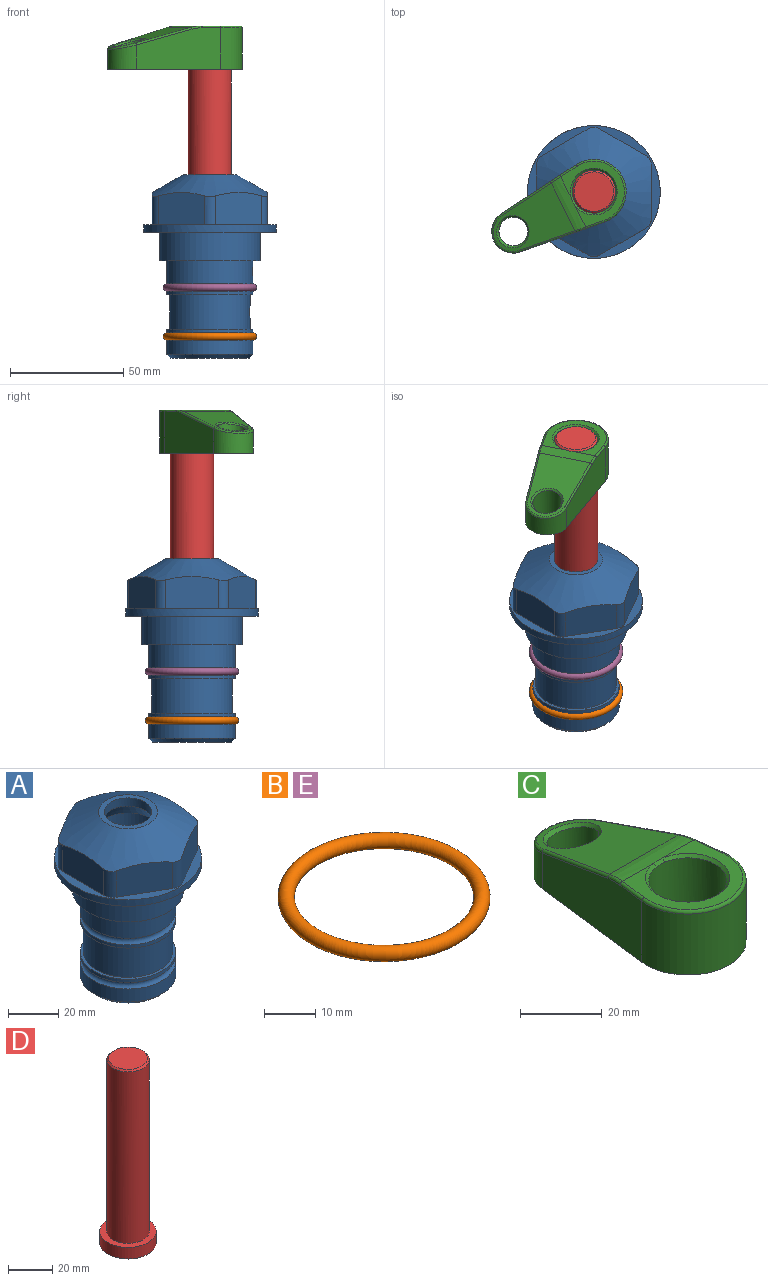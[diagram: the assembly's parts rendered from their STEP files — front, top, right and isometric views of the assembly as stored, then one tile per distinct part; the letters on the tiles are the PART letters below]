
ASSEMBLY  parts=5 mates=4
PART A: 36 faces, bbox 58.7x58.7x81 mm
  f0: cylinder r=17.78mm len=35.56mm, axis (0,0,1), area 1670.8mm2, adj f23,f24,f31
  f1: cylinder r=19.05mm len=38.1mm, axis (0,0,1), area 1191.9mm2, adj f26,f27,f30
  f2: plane 58.66x58.66mm, normal (0,0,-1), area 1150.6mm2, adj f3,f28
  f3: cylinder r=29.33mm len=58.66mm, axis (0,0,-1), area 585.1mm2, adj f2,f4
  f4: plane 58.66x58.66mm, normal (0,0,1), area 475.9mm2, adj f3,f5,f6,f7,f8,f9,f10,f11
  f5: plane 20.32x14.34mm, normal (-0.5,0.87,0), area 324.4mm2, adj f4,f15,f16,f17
  f6: plane 20.32x14.34mm, normal (0.5,0.87,0), area 324.4mm2, adj f4,f14,f15,f17
  f7: plane 23.48x14.34mm, normal (1,0,0), area 324.4mm2, adj f4,f13,f14,f17
  f8: plane 20.32x14.34mm, normal (0.5,-0.87,0), area 324.4mm2, adj f4,f12,f13,f17
  f9: plane 20.32x14.34mm, normal (-0.5,-0.87,0), area 324.4mm2, adj f4,f11,f12,f17
  f10: plane 23.48x14.34mm, normal (-1,0,0), area 324.4mm2, adj f4,f11,f16,f17
  f11: cylinder r=5.08mm len=12.85mm, axis (0,0,-1), area 67.2mm2, adj f4,f9,f10,f17
  f12: cylinder r=5.08mm len=12.85mm, axis (0,0,-1), area 67.2mm2, adj f4,f8,f9,f17
  f13: cylinder r=5.08mm len=12.85mm, axis (0,0,-1), area 67.2mm2, adj f4,f7,f8,f17
  f14: cylinder r=5.08mm len=12.85mm, axis (0,0,-1), area 67.2mm2, adj f4,f6,f7,f17
  f15: cylinder r=5.08mm len=12.85mm, axis (0,0,-1), area 67.2mm2, adj f4,f5,f6,f17
  f16: cylinder r=5.08mm len=12.85mm, axis (0,0,-1), area 67.2mm2, adj f4,f5,f10,f17
  f17: cone r=11.73mm half-angle=60deg, axis (0,0,-1), area 2071.8mm2, adj f5,f6,f7,f8,f9,f10,f11,f12
  f18: plane 23.46x23.46mm, normal (0,0,1), area 147.4mm2, adj f17,f35
  f19: plane 34.93x34.93mm, normal (0,0,-1), area 958mm2, adj f29
  f20: cylinder r=19.05mm len=38.1mm, axis (0,0,1), area 760.1mm2, adj f21,f29
  f21: torus R=19.05mm, axis (0,0,1), area 565.3mm2, adj f20,f22
  f22: cylinder r=19.05mm len=38.1mm, axis (0,0,1), area 190mm2, adj f21,f23
  f23: plane 38.1x38.1mm, normal (0,0,1), area 146.9mm2, adj f0,f22
  f24: plane 38.1x38.1mm, normal (0,0,-1), area 146.9mm2, adj f0,f25
  f25: cylinder r=19.05mm len=38.1mm, axis (0,0,1), area 190mm2, adj f24,f26
  f26: torus R=19.05mm, axis (0,0,1), area 565.3mm2, adj f1,f25
  f27: plane 44.45x44.45mm, normal (0,0,-1), area 411.7mm2, adj f1,f28
  f28: cylinder r=22.23mm len=44.45mm, axis (0,0,1), area 1773.5mm2, adj f2,f27
  f29: cone r=19.05mm half-angle=45deg, axis (0,0,1), area 257.5mm2, adj f19,f20
  f30: cylinder r=3.17mm len=6.75mm, axis (-1,0,0), area 128mm2, adj f1,f33
  f31: cylinder r=3.17mm len=6.35mm, axis (-1,0,0), area 102.5mm2, adj f0,f33
  f32: plane 25.4x25.4mm, normal (0,0,1), area 506.7mm2, adj f33
  f33: cylinder r=12.7mm len=66.42mm, axis (0,0,-1), area 5236.2mm2, adj f30,f31,f32,f34
  f34: cone r=9.53mm half-angle=30deg, axis (0,0,-1), area 443.4mm2, adj f33,f35
  f35: cylinder r=9.53mm len=19.05mm, axis (0,0,-1), area 240.9mm2, adj f18,f34
PART B: 1 faces, bbox 44.7x44.7x3.2 mm
  f0: torus R=19.05mm, axis (0,0,1), area 1193.9mm2
PART C: 31 faces, bbox 31.7x65.5x19.8 mm
  f0: plane 39.12x18.26mm, normal (0.99,0.12,0), area 612.2mm2, adj f1,f4,f7,f11,f13,f15
  f1: cylinder r=9.53mm len=18.91mm, axis (0,0,-1), area 296.1mm2, adj f0,f2,f7,f17
  f2: plane 39.12x18.26mm, normal (-0.99,0.12,0), area 612.2mm2, adj f1,f4,f7,f12,f14,f16
  f3: cylinder r=6.35mm len=12.7mm, axis (0,0,-1), area 362.4mm2, adj f7,f18
  f4: cylinder r=14.29mm len=28.58mm, axis (0,0,-1), area 882.2mm2, adj f0,f2,f7,f10
  f5: cylinder r=9.53mm len=19.05mm, axis (0,0,-1), area 1092.6mm2, adj f7,f19,f20
  f6: plane 26.99x23.69mm, normal (0,0,1), area 216.2mm2, adj f9,f10,f11,f12,f19
  f7: plane 63.5x28.58mm, normal (0,0,-1), area 661.8mm2, adj f0,f1,f2,f3,f4,f5,f22,f23
  f8: plane 33.52x23.6mm, normal (0,0.26,0.97), area 486mm2, adj f9,f15,f16,f17,f18
  f9: cylinder r=19.05mm len=24.72mm, axis (1,0,0), area 120.4mm2, adj f6,f8,f13,f14,f20
  f10: torus R=13.49mm, axis (0,0,1), area 59mm2, adj f4,f6,f11,f12
  f11: cylinder r=0.79mm len=8.67mm, axis (0.12,-0.99,0), area 10.8mm2, adj f0,f6,f10,f13
  f12: cylinder r=0.79mm len=8.67mm, axis (0.12,0.99,0), area 10.8mm2, adj f2,f6,f10,f14
  f13: bspline ~4.95x1.42mm, area 6.1mm2, adj f0,f9,f11,f15
  f14: bspline ~4.95x1.42mm, area 6.1mm2, adj f2,f9,f12,f16
  f15: cylinder r=0.79mm len=25.95mm, axis (0.12,-0.96,0.26), area 32.9mm2, adj f0,f8,f13,f17
  f16: cylinder r=0.79mm len=25.95mm, axis (0.12,0.96,-0.26), area 32.9mm2, adj f2,f8,f14,f17
  f17: bspline ~18.91x8.38mm, area 30mm2, adj f1,f8,f15,f16
  f18: bspline ~14.29x14.29mm, area 48.3mm2, adj f3,f8
  f19: cone r=9.53mm half-angle=45deg, axis (0,0,1), area 66.5mm2, adj f5,f6,f20
  f20: bspline ~3.22x0.96mm, area 3.5mm2, adj f5,f9,f19
  f21: plane 2.75x2.72mm, normal (0,0,-1), area 2.9mm2, adj f23,f25,f28
  f22: plane 23.05x15.88mm, normal (-0.99,-0.12,0), area 323.6mm2, adj f7,f25,f26,f27,f28,f29
  f23: plane 23.05x15.88mm, normal (0.99,-0.12,0), area 323.6mm2, adj f7,f21,f25,f27,f28,f30
  f24: cylinder r=9.53mm len=10.69mm, axis (0,0,-1), area 114.7mm2, adj f7,f27,f29,f30
  f25: cylinder r=12.7mm len=20.59mm, axis (0,0,-1), area 381.1mm2, adj f7,f21,f22,f23,f26,f28
  f26: plane 2.75x2.72mm, normal (0,0,-1), area 2.9mm2, adj f22,f25,f28
  f27: plane 19.72x18.37mm, normal (0,-0.26,-0.97), area 291.8mm2, adj f22,f23,f24,f28,f29,f30
  f28: cylinder r=15.88mm len=19.92mm, axis (1,0,0), area 54.8mm2, adj f21,f22,f23,f25,f26,f27
  f29: cylinder r=1.59mm len=11mm, axis (0,0,-1), area 34.7mm2, adj f7,f22,f24,f27
  f30: cylinder r=1.59mm len=11mm, axis (0,0,-1), area 34.7mm2, adj f7,f23,f24,f27
PART D: 6 faces, bbox 25.4x25.4x101.6 mm
  f0: plane 17.46x17.46mm, normal (0,0,1), area 239.5mm2, adj f5
  f1: plane 25.4x25.4mm, normal (0,0,-1), area 506.7mm2, adj f2
  f2: cylinder r=12.7mm len=25.4mm, axis (0,0,1), area 506.7mm2, adj f1,f3
  f3: plane 25.4x25.4mm, normal (0,0,1), area 221.7mm2, adj f2,f4
  f4: cylinder r=9.53mm len=94.46mm, axis (0,0,1), area 5653mm2, adj f3,f5
  f5: cone r=8.73mm half-angle=45deg, axis (0,0,-1), area 64.4mm2, adj f0,f4
PART E: same geometry as B
PLACE A at identity fixed
PLACE B t=(0,0,-21.59)mm
PLACE C rot(axis=(0,0,1),116.3deg) t=(0,0,27.55)mm
PLACE D rot(axis=(0,0,1),116.3deg) t=(0,0,27.55)mm
PLACE E at identity
MATE fastened D.f2 <-> C.f4  axis (0,0,1) through (0,0,91.05)mm
MATE fastened E.f0 <-> A.f0  axis (0,0,1) through (0,0,-24.51)mm
MATE fastened B.f0 <-> A.f0  axis (0,0,1) through (0,0,-46.1)mm
MATE cylindrical A.f0 <-> D.f2  axis (0,0,1) through (0,0,-50.55)mm
